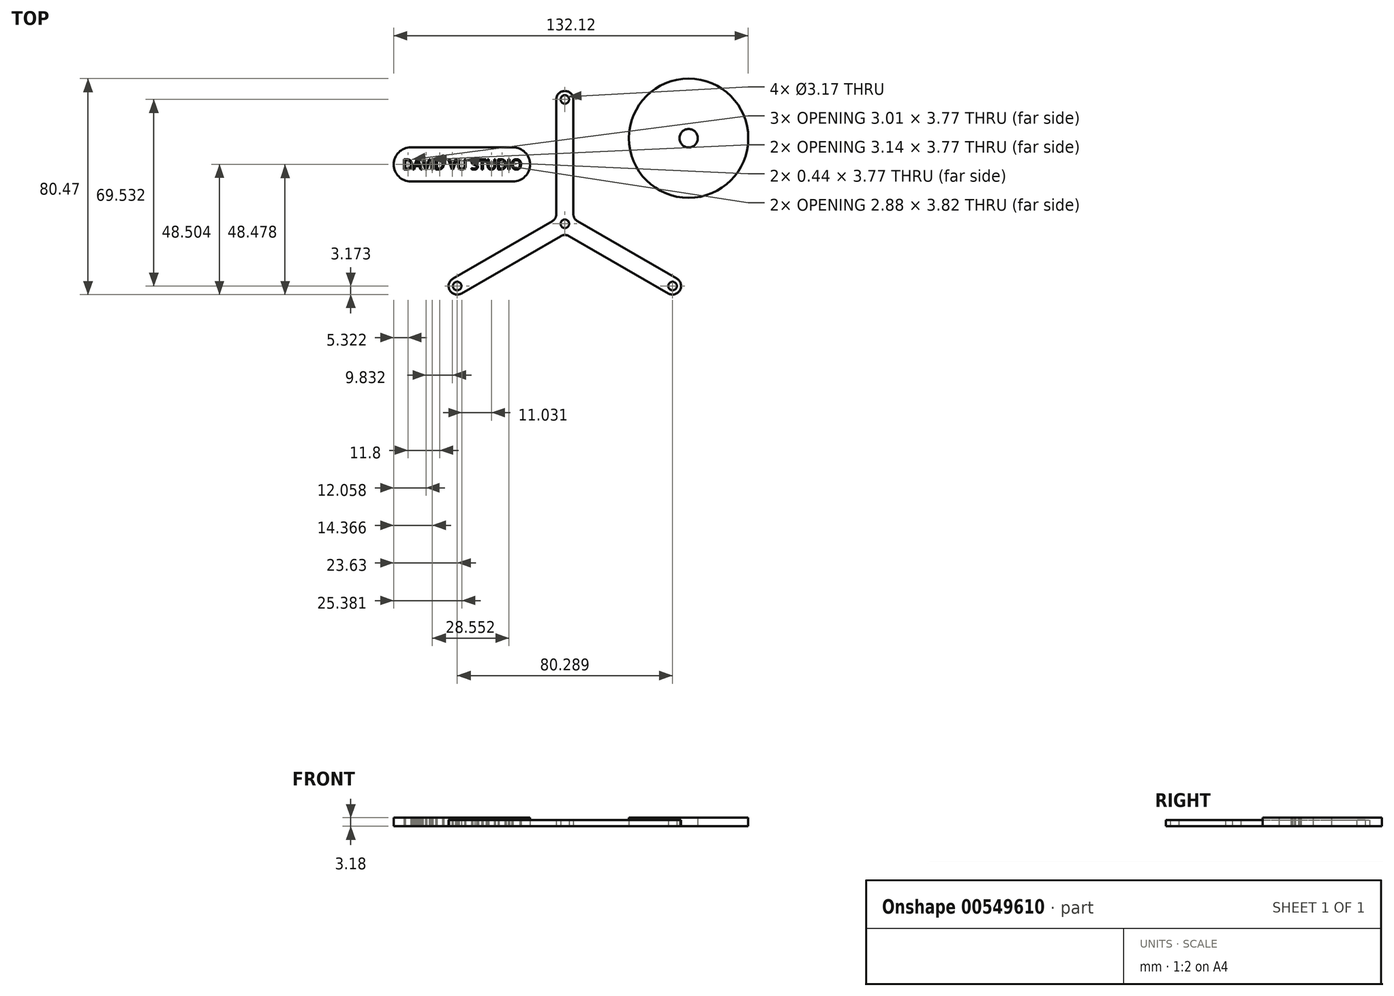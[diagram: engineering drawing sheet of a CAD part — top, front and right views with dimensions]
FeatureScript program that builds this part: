
annotation { "Feature Type Name" : "Feature", "Feature Type Description" : "" }
export const myFeature = defineFeature(function(context is Context, id is Id, definition is map)
    precondition{}
    {
        {
            var Q0;
            Q0=qCreatedBy(makeId("Top.planeOp"),FACE);
            var sketch = newSketch(context, id + "F0", { "sketchPlane" : qUnion([Q0])});
            skLineSegment(sketch, "E0.left", {"start": v(0, 3.67) * mm, "end": v(0, 46.35) * mm});
            skLineSegment(sketch, "E0.right", {"start": v(6.35, 3.67) * mm, "end": v(6.35, 46.35) * mm});
            skArc(sketch, "E1", {"start": v(0, 46.35) * mm, "mid": v(3.17, 49.53) * mm, "end": v(6.35, 46.35) * mm});
            skCircle(sketch, "E2", {"center": v(3.17, 46.35) * mm, "radius": 1.59 * mm});
            skLineSegment(sketch, "E3.1.0", {"start": v(-1.59, 0.92) * mm, "end": v(-38.56, -20.43) * mm});
            skLineSegment(sketch, "E3.1.1", {"start": v(1.59, -4.58) * mm, "end": v(-35.38, -25.93) * mm});
            skArc(sketch, "E3.1.3", {"start": v(-35.38, -25.93) * mm, "mid": v(-39.72, -24.77) * mm, "end": v(-38.56, -20.43) * mm});
            skCircle(sketch, "E3.1.4", {"center": v(-36.97, -23.18) * mm, "radius": 1.59 * mm});
            skLineSegment(sketch, "E3.2.0", {"start": v(4.76, -4.58) * mm, "end": v(41.73, -25.93) * mm});
            skLineSegment(sketch, "E3.2.1", {"start": v(7.94, 0.92) * mm, "end": v(44.9, -20.43) * mm});
            skArc(sketch, "E3.2.3", {"start": v(44.9, -20.43) * mm, "mid": v(46.07, -24.77) * mm, "end": v(41.73, -25.93) * mm});
            skCircle(sketch, "E3.2.4", {"center": v(43.32, -23.18) * mm, "radius": 1.59 * mm});
            skPoint(sketch, "E3.center", {"position": v(3.17, 0) * mm});
            skCircle(sketch, "E4", {"center": v(3.17, 0) * mm, "radius": 1.59 * mm});
            skPoint(sketch, "E5.visualSharp", {"position": v(6.35, 1.83) * mm});
            skArc(sketch, "E5.filletArc", {"start": v(6.35, 3.67) * mm, "mid": v(6.78, 2.08) * mm, "end": v(7.94, 0.92) * mm});
            skPoint(sketch, "E6.visualSharp", {"position": v(3.17, -3.67) * mm});
            skArc(sketch, "E6.filletArc", {"start": v(4.76, -4.58) * mm, "mid": v(3.17, -4.16) * mm, "end": v(1.59, -4.58) * mm});
            skPoint(sketch, "E7.visualSharp", {"position": v(0, 1.83) * mm});
            skArc(sketch, "E7.filletArc", {"start": v(-1.59, 0.92) * mm, "mid": v(-0.43, 2.08) * mm, "end": v(0, 3.67) * mm});
            skCircle(sketch, "E8", {"center": v(49.3, 31.9) * mm, "radius": 22.23 * mm});
            skCircle(sketch, "E9", {"center": v(49.3, 31.9) * mm, "radius": 3.43 * mm});
            skLineSegment(sketch, "E10.bottom", {"start": v(-54.25, 15.79) * mm, "end": v(-16.15, 15.79) * mm});
            skLineSegment(sketch, "E10.top", {"start": v(-54.25, 28.49) * mm, "end": v(-16.15, 28.49) * mm});
            skPoint(sketch, "E11", {"position": v(-54.25, 22.14) * mm});
            skPoint(sketch, "E12", {"position": v(-16.15, 22.14) * mm});
            skArc(sketch, "E13", {"start": v(-54.25, 15.79) * mm, "mid": v(-60.6, 22.14) * mm, "end": v(-54.25, 28.49) * mm});
            skArc(sketch, "E14", {"start": v(-16.15, 15.79) * mm, "mid": v(-9.8, 22.14) * mm, "end": v(-16.15, 28.49) * mm});
            skText(sketch, "E15", { "text": "DAVID VU STUDIO\n", "fontName": "OpenSans-Regular.ttf"});
            skCircle(sketch, "E16", {"center": v(-5.32, -32.13) * mm, "radius": 12.7 * mm});
            skText(sketch, "E17", { "text": "VU", "fontName": "Arimo-Regular.ttf"});
            const initialGuessF0  = {"E15": [-0.0573, 0.02027, 1, 0, 0.0038], "E17": [-0.0163, -0.03765, 1, 0, 0.01155]};
            skSetInitialGuess(sketch, initialGuessF0);
            skSolve(sketch);
        }
        {
            var Q0;
            Q0=makeQuery(id+"F0.imprint","IMPRINT",FACE,{"disambiguationData":[TD([[makeQuery(id+"F0.imprint","IMPRINT",EDGE,{"derivedFrom":sQuery(id+"F0.wireOp",EDGE,"E0.left")}),-1.0]])]});
            extrude(context, id + "F1", {"entities" : qUnion([Q0]), "depth" : 2.3 * mm, "offsetDistance" : 25.4 * mm});
        }
        {
            var Q0;
            Q0=makeQuery(id+"F0.imprint","IMPRINT",FACE,{"disambiguationData":[TD([[makeQuery(id+"F0.imprint","IMPRINT",EDGE,{"derivedFrom":sQuery(id+"F0.wireOp",EDGE,"E8")}),1.0]])]});
            extrude(context, id + "F2", {"entities" : qUnion([Q0]), "depth" : 3.17 * mm, "offsetDistance" : 25.4 * mm});
        }
        {
            var Q0;
            Q0=makeQuery(id+"F0.imprint","IMPRINT",FACE,{"disambiguationData":[TD([[makeQuery(id+"F0.imprint","IMPRINT",EDGE,{"derivedFrom":sQuery(id+"F0.wireOp",EDGE,"E10.bottom")}),1.0]])]});
            var Q1;
            Q1=makeQuery(id+"F0.imprint","IMPRINT",FACE,{"disambiguationData":[TD([[makeQuery(id+"F0.imprint","IMPRINT",EDGE,{"derivedFrom":sQuery(id+"F0.wireOp",EDGE,"E15.sketch_text.stroke-150")}),1.0]])]});
            var Q2;
            Q2=makeQuery(id+"F0.imprint","IMPRINT",FACE,{"disambiguationData":[TD([[makeQuery(id+"F0.imprint","IMPRINT",EDGE,{"derivedFrom":sQuery(id+"F0.wireOp",EDGE,"E15.sketch_text.stroke-131")}),1.0]])]});
            var Q3;
            Q3=makeQuery(id+"F0.imprint","IMPRINT",FACE,{"disambiguationData":[TD([[makeQuery(id+"F0.imprint","IMPRINT",EDGE,{"derivedFrom":sQuery(id+"F0.wireOp",EDGE,"E15.sketch_text.stroke-47")}),1.0]])]});
            var Q4;
            Q4=makeQuery(id+"F0.imprint","IMPRINT",FACE,{"disambiguationData":[TD([[makeQuery(id+"F0.imprint","IMPRINT",EDGE,{"derivedFrom":sQuery(id+"F0.wireOp",EDGE,"E15.sketch_text.stroke-7")}),1.0]])]});
            var Q5;
            Q5=makeQuery(id+"F0.imprint","IMPRINT",FACE,{"disambiguationData":[TD([[makeQuery(id+"F0.imprint","IMPRINT",EDGE,{"derivedFrom":sQuery(id+"F0.wireOp",EDGE,"E15.sketch_text.stroke-22")}),1.0]])]});
            extrude(context, id + "F3", {"entities" : qUnion([Q0, Q1, Q2, Q3, Q4, Q5]), "depth" : 3.17 * mm, "offsetDistance" : 25.4 * mm});
        }
    });
